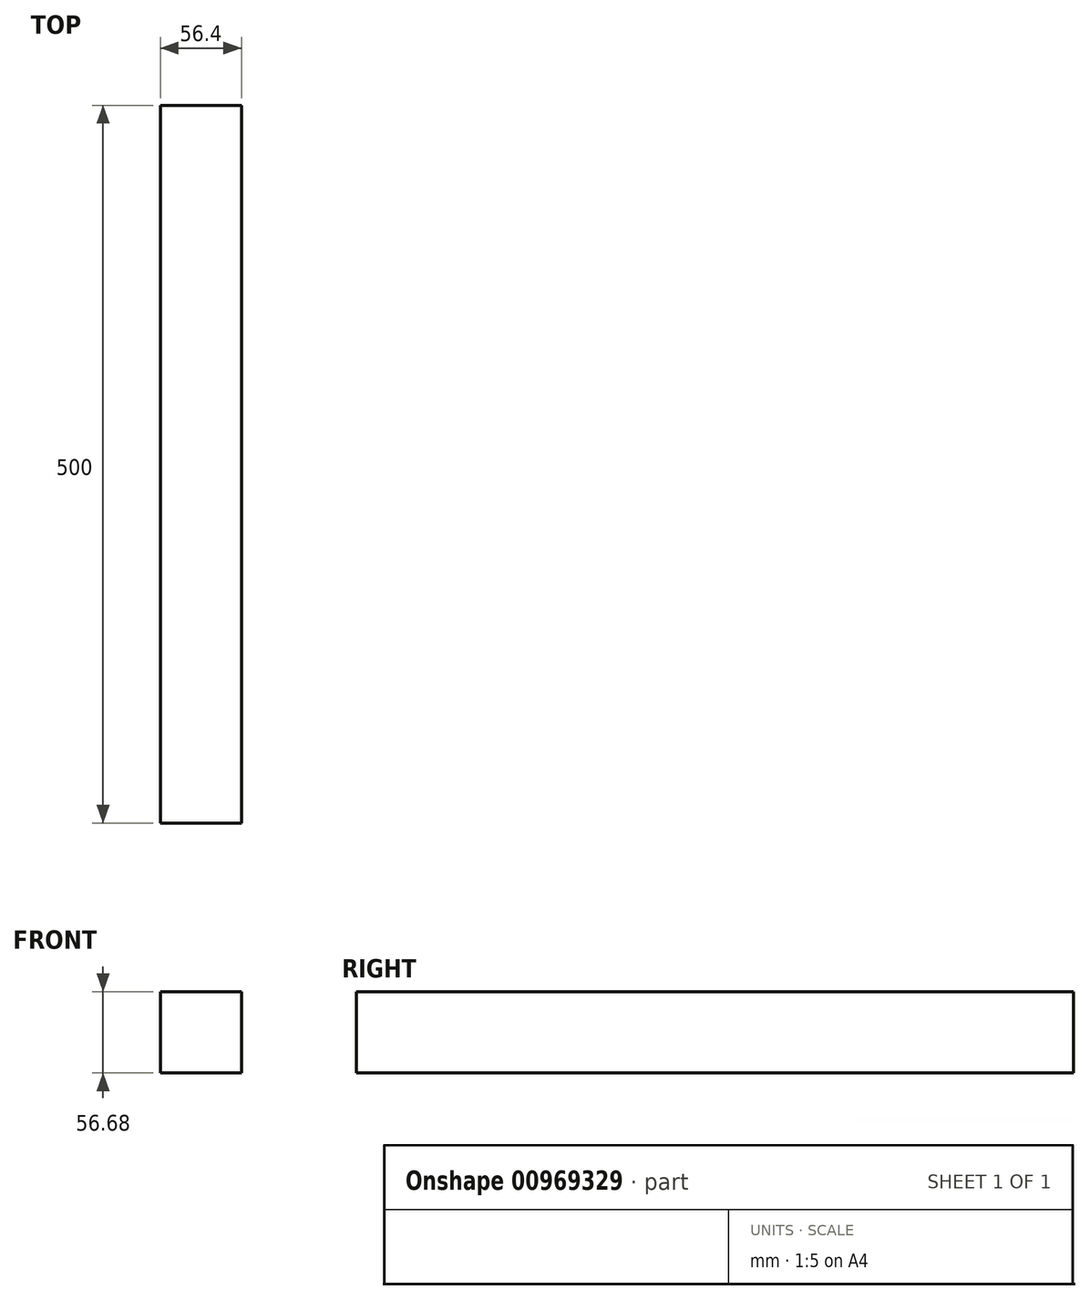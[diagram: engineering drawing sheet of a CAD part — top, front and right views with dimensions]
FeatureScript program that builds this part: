
annotation { "Feature Type Name" : "Feature", "Feature Type Description" : "" }
export const myFeature = defineFeature(function(context is Context, id is Id, definition is map)
    precondition{}
    {
        {
            var Q0;
            Q0=qCreatedBy(makeId("Front.planeOp"),FACE);
            var sketch = newSketch(context, id + "F0", { "sketchPlane" : qUnion([Q0])});
            skLineSegment(sketch, "E0", {"start": v(-26.94, 0) * mm, "end": v(-26.94, -27.9) * mm});
            skLineSegment(sketch, "E1", {"start": v(-26.94, -27.9) * mm, "end": v(29.46, -27.9) * mm});
            skLineSegment(sketch, "E2", {"start": v(29.46, -27.9) * mm, "end": v(29.46, 28.78) * mm});
            skLineSegment(sketch, "E3", {"start": v(29.46, 28.78) * mm, "end": v(-26.94, 28.78) * mm});
            skLineSegment(sketch, "E4", {"start": v(-26.94, 28.78) * mm, "end": v(-26.94, 0) * mm});
            skSolve(sketch);
        }
        {
            var Q0;
            Q0=makeQuery(id+"F0.imprint","IMPRINT",FACE,{"disambiguationData":[TD([[makeQuery(id+"F0.imprint","IMPRINT",EDGE,{"derivedFrom":sQuery(id+"F0.wireOp",EDGE,"E0")}),1.0]])]});
            extrude(context, id + "F1", {"entities" : qUnion([Q0]), "depth" : 500 * mm, "offsetDistance" : 25.4 * mm});
        }
    });
